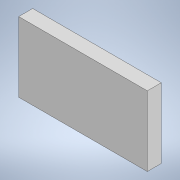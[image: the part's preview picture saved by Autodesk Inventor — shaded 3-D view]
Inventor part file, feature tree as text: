
AUTODESK INVENTOR PART (.ipt)
format: ipt  version: 2021 (Build 250183000, 183)  size: 88,576 bytes
history: native  units: mm
features: other x1, extrude x1, sketch x1
ambient origin geometry x8: Origin, YZ Plane, XZ Plane, XY Plane, X Axis, Y Axis, Z Axis, Center Point
bodies: Body1 (feature_tree)
feature tree (3):
  other  "ソリッド1"
  extrude  "押し出し1"  Depth=5000.0mm
  sketch  "スケッチ1"
